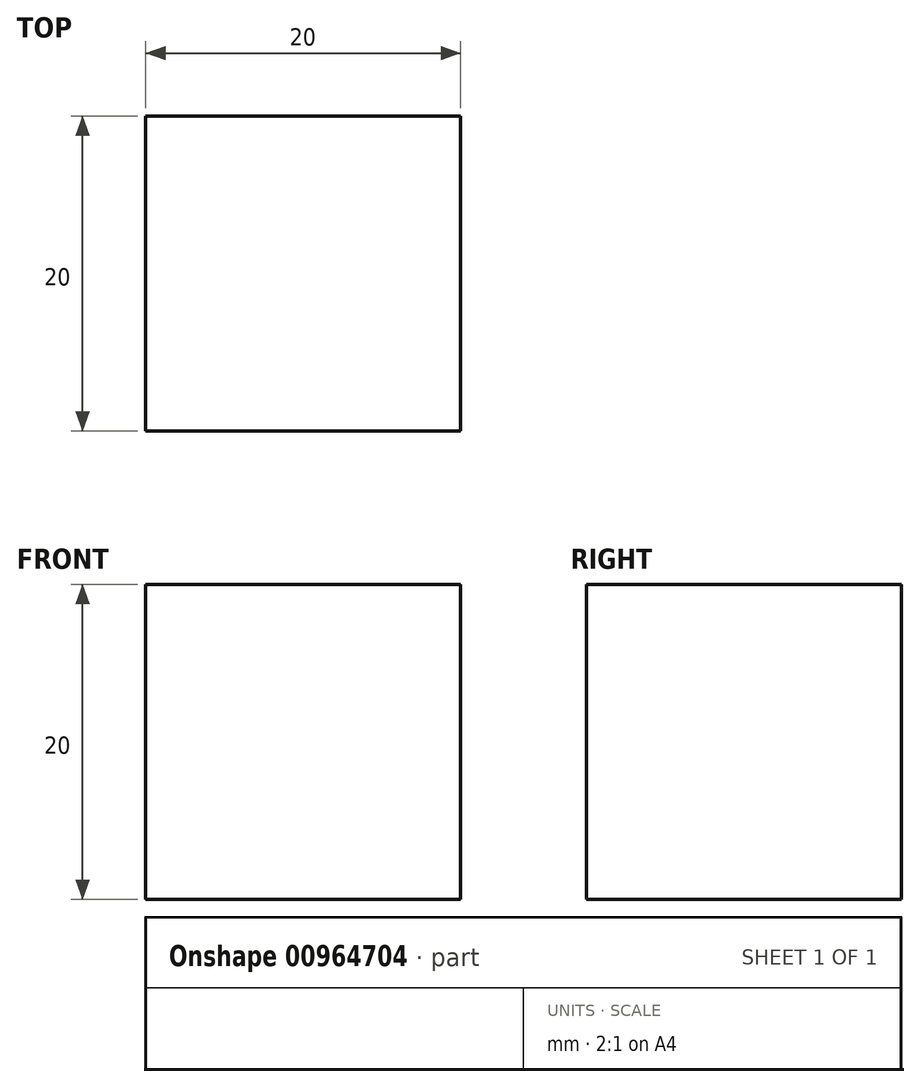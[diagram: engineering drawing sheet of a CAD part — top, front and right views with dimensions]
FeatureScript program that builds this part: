
annotation { "Feature Type Name" : "Feature", "Feature Type Description" : "" }
export const myFeature = defineFeature(function(context is Context, id is Id, definition is map)
    precondition{}
    {
        {
            var Q0;
            Q0=qCreatedBy(makeId("Top.planeOp"),FACE);
            var sketch = newSketch(context, id + "F0", { "sketchPlane" : qUnion([Q0])});
            skLineSegment(sketch, "E0.bottom", {"start": v(0, 20) * mm, "end": v(20, 20) * mm});
            skLineSegment(sketch, "E0.top", {"start": v(0, 0) * mm, "end": v(20, 0) * mm});
            skLineSegment(sketch, "E0.left", {"start": v(0, 20) * mm, "end": v(0, 0) * mm});
            skLineSegment(sketch, "E0.right", {"start": v(20, 20) * mm, "end": v(20, 0) * mm});
            skSolve(sketch);
        }
        {
            var Q0;
            Q0=makeQuery(id+"F0.imprint","IMPRINT",FACE,{"disambiguationData":[TD([[makeQuery(id+"F0.imprint","IMPRINT",EDGE,{"derivedFrom":sQuery(id+"F0.wireOp",EDGE,"E0.bottom")}),-1.0]])]});
            extrude(context, id + "F1", {"entities" : qUnion([Q0]), "flatOperationType" : FlatOperationType.REMOVE, "depth" : 20 * mm, "offsetDistance" : 25 * mm, "domain" : OperationDomain.MODEL});
        }
    });
